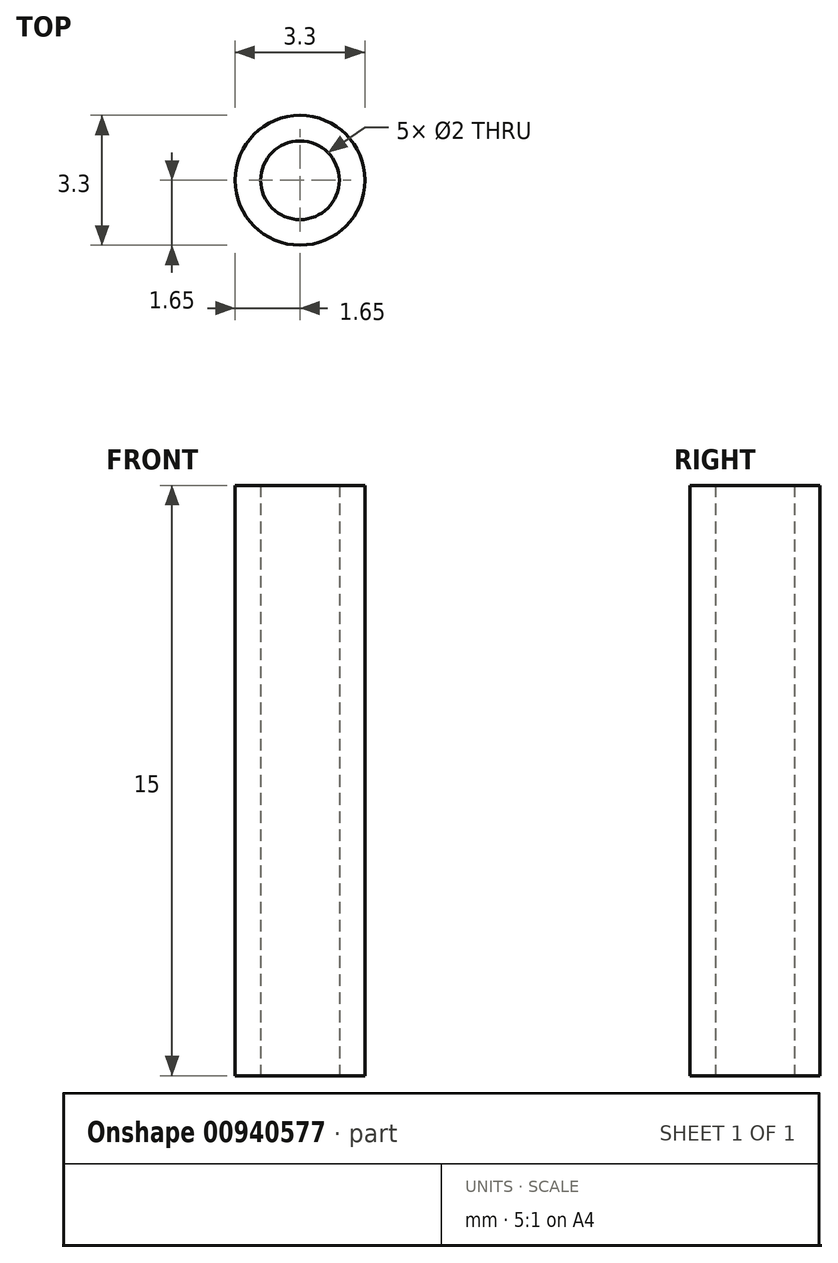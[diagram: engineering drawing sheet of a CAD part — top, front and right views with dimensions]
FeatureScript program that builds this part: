
annotation { "Feature Type Name" : "Feature", "Feature Type Description" : "" }
export const myFeature = defineFeature(function(context is Context, id is Id, definition is map)
    precondition{}
    {
        {
            var Q0;
            Q0=qCreatedBy(makeId("Top.planeOp"),FACE);
            var sketch = newSketch(context, id + "F0", { "sketchPlane" : qUnion([Q0])});
            skCircle(sketch, "E0", {"center": v(0, 0) * mm, "radius": 1.65 * mm});
            skCircle(sketch, "E1", {"center": v(0, 0) * mm, "radius": 1 * mm});
            skSolve(sketch);
        }
        {
            var Q0;
            Q0=makeQuery(id+"F0.imprint","IMPRINT",FACE,{"disambiguationData":[TD([[makeQuery(id+"F0.imprint","IMPRINT",EDGE,{"derivedFrom":sQuery(id+"F0.wireOp",EDGE,"E0")}),1.0]])]});
            extrude(context, id + "F1", {"entities" : qUnion([Q0]), "depth" : 15 * mm, "offsetDistance" : 25.4 * mm});
        }
    });
